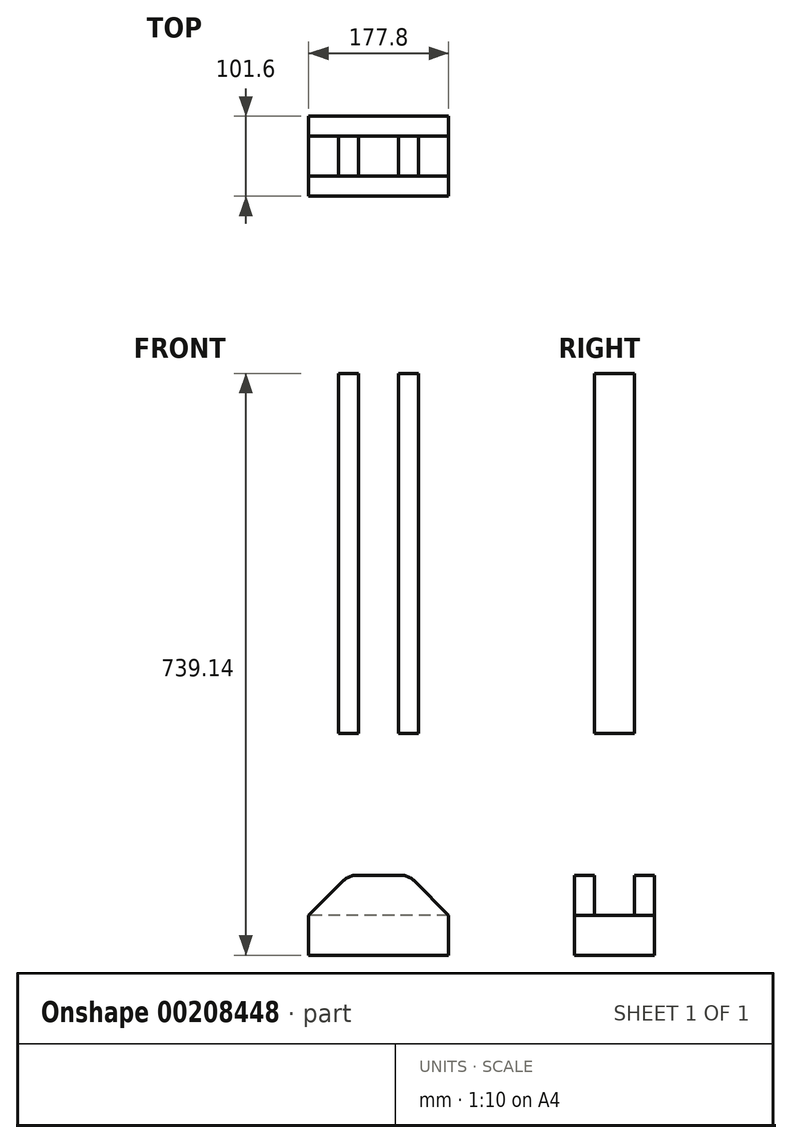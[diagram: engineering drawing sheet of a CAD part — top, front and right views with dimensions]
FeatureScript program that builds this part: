
annotation { "Feature Type Name" : "Feature", "Feature Type Description" : "" }
export const myFeature = defineFeature(function(context is Context, id is Id, definition is map)
    precondition{}
    {
        {
            var Q0;
            Q0=qCreatedBy(makeId("Front.planeOp"),FACE);
            var sketch = newSketch(context, id + "F0", { "sketchPlane" : qUnion([Q0])});
            skLineSegment(sketch, "E0.bottom", {"start": v(88.9, 76.2) * mm, "end": v(-88.9, 76.2) * mm});
            skLineSegment(sketch, "E0.top", {"start": v(88.9, -76.2) * mm, "end": v(-88.9, -76.2) * mm});
            skLineSegment(sketch, "E0.left", {"start": v(88.9, 76.2) * mm, "end": v(88.9, -76.2) * mm});
            skLineSegment(sketch, "E0.right", {"start": v(-88.9, 76.2) * mm, "end": v(-88.9, -76.2) * mm});
            skPoint(sketch, "E0.middle", {"position": v(0, 0) * mm});
            skSolve(sketch);
        }
        {
            var Q0;
            Q0=qSketchRegion(id+"F0",true);
            extrude(context, id + "F1", {"entities" : qUnion([Q0]), "endBound" : BoundingType.SYMMETRIC, "depth" : 101.6 * mm});
        }
        {
            var Q0;
            Q0=makeQuery(id+"F1.opExtrude","SWEPT_FACE",FACE,{"disambiguationData":[OSD([sQuery(id+"F0.wireOp",EDGE,"E0.bottom")])]});
            var sketch = newSketch(context, id + "F2", { "sketchPlane" : qUnion([Q0])});
            skLineSegment(sketch, "E1.bottom", {"start": v(88.9, 25.4) * mm, "end": v(-88.9, 25.4) * mm});
            skLineSegment(sketch, "E1.top", {"start": v(88.9, -25.4) * mm, "end": v(-88.9, -25.4) * mm});
            skLineSegment(sketch, "E1.left", {"start": v(88.9, 25.4) * mm, "end": v(88.9, -25.4) * mm});
            skLineSegment(sketch, "E1.right", {"start": v(-88.9, 25.4) * mm, "end": v(-88.9, -25.4) * mm});
            skPoint(sketch, "E1.middle", {"position": v(0, 0) * mm});
            skSolve(sketch);
        }
        {
            var Q0;
            Q0=qSketchRegion(id+"F2",true);
            extrude(context, id + "F3", {"entities" : qUnion([Q0]), "operationType" : NewBodyOperationType.REMOVE, "oppositeDirection" : true, "depth" : 50.8 * mm});
        }
        {
            var Q0;
            {var subQ0=sQuery(id+"F0.wireOp",EDGE,"E0.bottom");var subQ1=sQuery(id+"F0.wireOp",EDGE,"E0.left");Q0=makeQuery(id+"F3.boolean.opBoolean","SPLIT",EDGE,{"disambiguationData":[TD([makeQuery(id+"F3.opExtrude","SWEPT_FACE",FACE,{"disambiguationData":[OSD([sQuery(id+"F2.wireOp",EDGE,"E1.top")])]})])],"derivedFrom":makeQuery(id+"F1.opExtrude","SWEPT_EDGE",EDGE,{"disambiguationData":[OSD([subQ0,subQ1])]})});}
            var Q1;
            {var subQ0=sQuery(id+"F0.wireOp",EDGE,"E0.bottom");var subQ1=sQuery(id+"F0.wireOp",EDGE,"E0.left");Q1=makeQuery(id+"F3.boolean.opBoolean","SPLIT",EDGE,{"disambiguationData":[TD([makeQuery(id+"F3.opExtrude","SWEPT_FACE",FACE,{"disambiguationData":[OSD([sQuery(id+"F2.wireOp",EDGE,"E1.bottom")])]})])],"derivedFrom":makeQuery(id+"F1.opExtrude","SWEPT_EDGE",EDGE,{"disambiguationData":[OSD([subQ0,subQ1])]})});}
            var Q2;
            {var subQ0=sQuery(id+"F0.wireOp",EDGE,"E0.bottom");var subQ1=sQuery(id+"F0.wireOp",EDGE,"E0.right");Q2=makeQuery(id+"F3.boolean.opBoolean","SPLIT",EDGE,{"disambiguationData":[TD([makeQuery(id+"F3.opExtrude","SWEPT_FACE",FACE,{"disambiguationData":[OSD([sQuery(id+"F2.wireOp",EDGE,"E1.bottom")])]})])],"derivedFrom":makeQuery(id+"F1.opExtrude","SWEPT_EDGE",EDGE,{"disambiguationData":[OSD([subQ0,subQ1])]})});}
            var Q3;
            {var subQ0=sQuery(id+"F0.wireOp",EDGE,"E0.bottom");var subQ1=sQuery(id+"F0.wireOp",EDGE,"E0.right");Q3=makeQuery(id+"F3.boolean.opBoolean","SPLIT",EDGE,{"disambiguationData":[TD([makeQuery(id+"F3.opExtrude","SWEPT_FACE",FACE,{"disambiguationData":[OSD([sQuery(id+"F2.wireOp",EDGE,"E1.top")])]})])],"derivedFrom":makeQuery(id+"F1.opExtrude","SWEPT_EDGE",EDGE,{"disambiguationData":[OSD([subQ0,subQ1])]})});}
            chamfer(context, id + "F4", {"entities" : qUnion([Q0, Q1, Q2, Q3]), "width" : 50.8 * mm, "tangentPropagation" : true});
        }
        {
            var Q0;
            {var subQ0=sQuery(id+"F0.wireOp",EDGE,"E0.right");var subQ2=sQuery(id+"F0.wireOp",EDGE,"E0.bottom");var subQ5=makeQuery(id+"F3.opExtrude","SWEPT_FACE",FACE,{"disambiguationData":[OSD([sQuery(id+"F2.wireOp",EDGE,"E1.top")])]});var subQ6=makeQuery(id+"F1.opExtrude","SWEPT_FACE",FACE,{"disambiguationData":[OSD([subQ2])]});Q0=makeQuery(id+"F4.opChamfer","BLEND_EDGE",EDGE,{"blendedFrom":[makeQuery(id+"F3.boolean.opBoolean","SPLIT",EDGE,{"disambiguationData":[TD([subQ5])],"derivedFrom":makeQuery(id+"F1.opExtrude","SWEPT_EDGE",EDGE,{"disambiguationData":[OSD([subQ2,subQ0])]})}),makeQuery(id+"F3.boolean.opBoolean","SPLIT",FACE,{"disambiguationData":[TD([subQ5])],"derivedFrom":subQ6})],"blendedInto":[makeQuery(id+"F3.boolean.opBoolean","SPLIT",FACE,{"disambiguationData":[TD([subQ5])],"derivedFrom":subQ6})]});}
            var Q1;
            {var subQ0=sQuery(id+"F0.wireOp",EDGE,"E0.right");var subQ2=sQuery(id+"F0.wireOp",EDGE,"E0.bottom");var subQ4=makeQuery(id+"F3.opExtrude","SWEPT_FACE",FACE,{"disambiguationData":[OSD([sQuery(id+"F2.wireOp",EDGE,"E1.bottom")])]});var subQ6=makeQuery(id+"F1.opExtrude","SWEPT_FACE",FACE,{"disambiguationData":[OSD([subQ2])]});Q1=makeQuery(id+"F4.opChamfer","BLEND_EDGE",EDGE,{"blendedFrom":[makeQuery(id+"F3.boolean.opBoolean","SPLIT",EDGE,{"disambiguationData":[TD([subQ4])],"derivedFrom":makeQuery(id+"F1.opExtrude","SWEPT_EDGE",EDGE,{"disambiguationData":[OSD([subQ2,subQ0])]})}),makeQuery(id+"F3.boolean.opBoolean","SPLIT",FACE,{"disambiguationData":[TD([subQ4])],"derivedFrom":subQ6})],"blendedInto":[makeQuery(id+"F3.boolean.opBoolean","SPLIT",FACE,{"disambiguationData":[TD([subQ4])],"derivedFrom":subQ6})]});}
            var Q2;
            {var subQ1=sQuery(id+"F0.wireOp",EDGE,"E0.left");var subQ2=sQuery(id+"F0.wireOp",EDGE,"E0.bottom");var subQ4=makeQuery(id+"F3.opExtrude","SWEPT_FACE",FACE,{"disambiguationData":[OSD([sQuery(id+"F2.wireOp",EDGE,"E1.bottom")])]});var subQ6=makeQuery(id+"F1.opExtrude","SWEPT_FACE",FACE,{"disambiguationData":[OSD([subQ2])]});Q2=makeQuery(id+"F4.opChamfer","BLEND_EDGE",EDGE,{"blendedFrom":[makeQuery(id+"F3.boolean.opBoolean","SPLIT",EDGE,{"disambiguationData":[TD([subQ4])],"derivedFrom":makeQuery(id+"F1.opExtrude","SWEPT_EDGE",EDGE,{"disambiguationData":[OSD([subQ2,subQ1])]})}),makeQuery(id+"F3.boolean.opBoolean","SPLIT",FACE,{"disambiguationData":[TD([subQ4])],"derivedFrom":subQ6})],"blendedInto":[makeQuery(id+"F3.boolean.opBoolean","SPLIT",FACE,{"disambiguationData":[TD([subQ4])],"derivedFrom":subQ6})]});}
            var Q3;
            {var subQ1=sQuery(id+"F0.wireOp",EDGE,"E0.left");var subQ2=sQuery(id+"F0.wireOp",EDGE,"E0.bottom");var subQ5=makeQuery(id+"F3.opExtrude","SWEPT_FACE",FACE,{"disambiguationData":[OSD([sQuery(id+"F2.wireOp",EDGE,"E1.top")])]});var subQ6=makeQuery(id+"F1.opExtrude","SWEPT_FACE",FACE,{"disambiguationData":[OSD([subQ2])]});Q3=makeQuery(id+"F4.opChamfer","BLEND_EDGE",EDGE,{"blendedFrom":[makeQuery(id+"F3.boolean.opBoolean","SPLIT",EDGE,{"disambiguationData":[TD([subQ5])],"derivedFrom":makeQuery(id+"F1.opExtrude","SWEPT_EDGE",EDGE,{"disambiguationData":[OSD([subQ2,subQ1])]})}),makeQuery(id+"F3.boolean.opBoolean","SPLIT",FACE,{"disambiguationData":[TD([subQ5])],"derivedFrom":subQ6})],"blendedInto":[makeQuery(id+"F3.boolean.opBoolean","SPLIT",FACE,{"disambiguationData":[TD([subQ5])],"derivedFrom":subQ6})]});}
            fillet(context, id + "F5", {"entities" : qUnion([Q0, Q1, Q2, Q3]), "radius" : 25.4 * mm, "tangentPropagation" : true, "allowEdgeOverflow" : false});
        }
        {
            var Q0;
            Q0=qCreatedBy(makeId("Front.planeOp"),FACE);
            var sketch = newSketch(context, id + "F6", { "sketchPlane" : qUnion([Q0])});
            skLineSegment(sketch, "E2", {"start": v(0, 38.1) * mm, "end": v(50.8, 38.1) * mm});
            skLineSegment(sketch, "E3", {"start": v(50.8, 38.1) * mm, "end": v(25.4, 38.1) * mm});
            skLineSegment(sketch, "E4", {"start": v(-25.4, 38.1) * mm, "end": v(-50.8, 38.1) * mm});
            skLineSegment(sketch, "E5", {"start": v(-50.8, 38.1) * mm, "end": v(-50.8, 495.3) * mm});
            skLineSegment(sketch, "E6", {"start": v(50.8, 38.1) * mm, "end": v(50.8, 495.3) * mm});
            skLineSegment(sketch, "E7.bottom", {"start": v(-50.8, 495.3) * mm, "end": v(-25.4, 495.3) * mm});
            skLineSegment(sketch, "E7.top", {"start": v(-50.8, 38.1) * mm, "end": v(-25.4, 38.1) * mm});
            skLineSegment(sketch, "E7.left", {"start": v(-50.8, 495.3) * mm, "end": v(-50.8, 38.1) * mm});
            skLineSegment(sketch, "E7.right", {"start": v(-25.4, 495.3) * mm, "end": v(-25.4, 38.1) * mm});
            skLineSegment(sketch, "E8.bottom", {"start": v(50.8, 495.3) * mm, "end": v(25.4, 495.3) * mm});
            skLineSegment(sketch, "E8.left", {"start": v(50.8, 495.3) * mm, "end": v(50.8, 38.1) * mm});
            skLineSegment(sketch, "E8.right", {"start": v(25.4, 495.3) * mm, "end": v(25.4, 38.1) * mm});
            skSolve(sketch);
        }
        {
            var Q0;
            Q0=qSketchRegion(id+"F6",true);
            extrude(context, id + "F7", {"entities" : qUnion([Q0]), "endBound" : BoundingType.SYMMETRIC, "depth" : 50.8 * mm});
        }
        {
            var Q0;
            Q0=makeQuery(id+"F7.opExtrude","SWEPT_BODY",BODY,{"disambiguationData":[OSD([sQuery(id+"F6.wireOp",EDGE,"E7.bottom"),sQuery(id+"F6.wireOp",EDGE,"E7.top"),sQuery(id+"F6.wireOp",EDGE,"E7.left"),sQuery(id+"F6.wireOp",EDGE,"E7.right")])]});
            var Q1;
            Q1=makeQuery(id+"F7.opExtrude","SWEPT_BODY",BODY,{"disambiguationData":[OSD([sQuery(id+"F6.wireOp",EDGE,"E8.bottom"),sQuery(id+"F6.wireOp",EDGE,"E3"),sQuery(id+"F6.wireOp",EDGE,"E8.left"),sQuery(id+"F6.wireOp",EDGE,"E8.right")])]});
            transform(context, id + "F8", {"entities" : qUnion([Q0, Q1]), "transformType" : TransformType.TRANSLATION_3D, "dx" : 0 * mm, "dy" : 0 * mm, "dz" : 218.44 * mm, "makeCopy" : false});
        }
        {
            var Q0;
            Q0=makeQuery(id+"F1.opExtrude","SWEPT_FACE",FACE,{"disambiguationData":[OSD([sQuery(id+"F0.wireOp",EDGE,"E0.top")])]});
            extrude(context, id + "F9", {"entities" : qUnion([Q0]), "operationType" : NewBodyOperationType.REMOVE, "oppositeDirection" : true, "depth" : 50.8 * mm});
        }
    });
